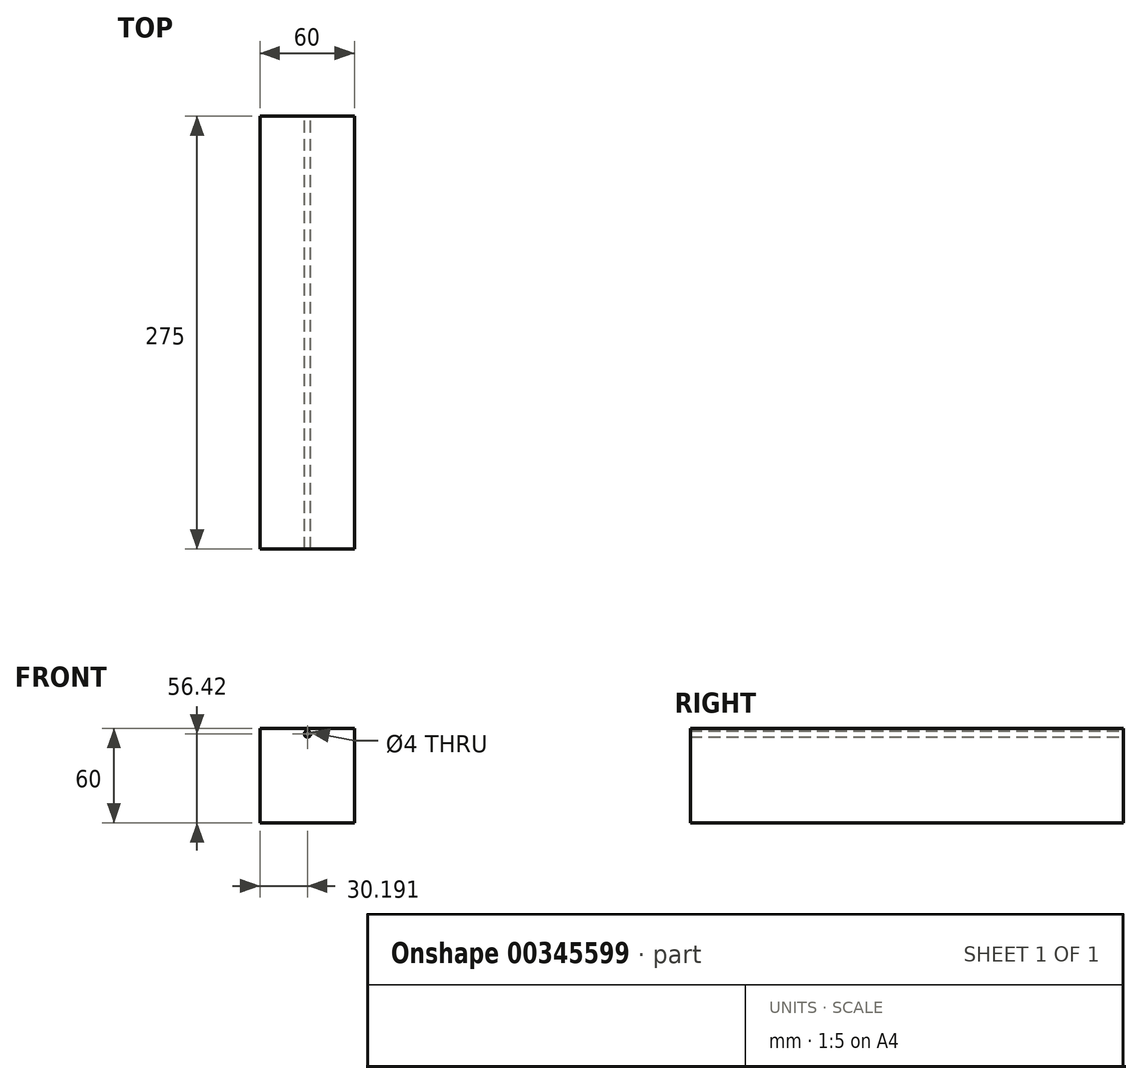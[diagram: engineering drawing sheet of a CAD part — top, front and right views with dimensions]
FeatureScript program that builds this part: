
annotation { "Feature Type Name" : "Feature", "Feature Type Description" : "" }
export const myFeature = defineFeature(function(context is Context, id is Id, definition is map)
    precondition{}
    {
        {
            var Q0;
            Q0=qCreatedBy(makeId("Front.planeOp"),FACE);
            var sketch = newSketch(context, id + "F0", { "sketchPlane" : qUnion([Q0])});
            skLineSegment(sketch, "E0.bottom", {"start": v(-28.85, 18.13) * mm, "end": v(31.15, 18.13) * mm});
            skLineSegment(sketch, "E0.top", {"start": v(-28.85, -41.87) * mm, "end": v(31.15, -41.87) * mm});
            skLineSegment(sketch, "E0.left", {"start": v(-28.85, 18.13) * mm, "end": v(-28.85, -41.87) * mm});
            skLineSegment(sketch, "E0.right", {"start": v(31.15, 18.13) * mm, "end": v(31.15, -41.87) * mm});
            skSolve(sketch);
        }
        {
            var Q0;
            Q0=qSketchRegion(id+"F0",true);
            extrude(context, id + "F1", {"entities" : qUnion([Q0]), "depth" : 25 * mm});
        }
        {
            var Q0;
            Q0=makeQuery(id+"F1.opExtrude","CAP_FACE",FACE,{"disambiguationData":[OSD([sQuery(id+"F0.wireOp",EDGE,"E0.bottom"),sQuery(id+"F0.wireOp",EDGE,"E0.top"),sQuery(id+"F0.wireOp",EDGE,"E0.left"),sQuery(id+"F0.wireOp",EDGE,"E0.right")])],"isStart":false});
            extrude(context, id + "F2", {"entities" : qUnion([Q0]), "operationType" : NewBodyOperationType.ADD, "depth" : 250 * mm});
        }
        {
            var Q0;
            Q0=qCreatedBy(makeId("Front.planeOp"),FACE);
            var sketch = newSketch(context, id + "F3", { "sketchPlane" : qUnion([Q0])});
            skPoint(sketch, "E1.center.orphan", {"position": v(0, 15.22) * mm});
            skCircle(sketch, "E2", {"center": v(1.34, 14.55) * mm, "radius": 2 * mm});
            skPoint(sketch, "E3.orphan", {"position": v(-28.66, 14.55) * mm});
            skSolve(sketch);
        }
        {
            var Q0;
            Q0=sQuery(id+"F3.wireOp",VERTEX,"E2.center");
            var Q1;
            Q1=makeQuery(id+"F1.opExtrude","SWEPT_BODY",BODY,{"disambiguationData":[OSD([sQuery(id+"F0.wireOp",EDGE,"E0.bottom"),sQuery(id+"F0.wireOp",EDGE,"E0.top"),sQuery(id+"F0.wireOp",EDGE,"E0.left"),sQuery(id+"F0.wireOp",EDGE,"E0.right")])]});
            hole(context, id + "F4", {"style" : HoleStyle.SIMPLE, "endStyle" : HoleEndStyle.THROUGH, "oppositeDirection" : true, "holeDiameter" : 4 * mm, "isTappedThrough" : true, "tappedDepth" : 12 * mm, "tapClearance" : 3, "locations" : qUnion([Q0]), "scope" : qUnion([Q1])});
        }
    });
